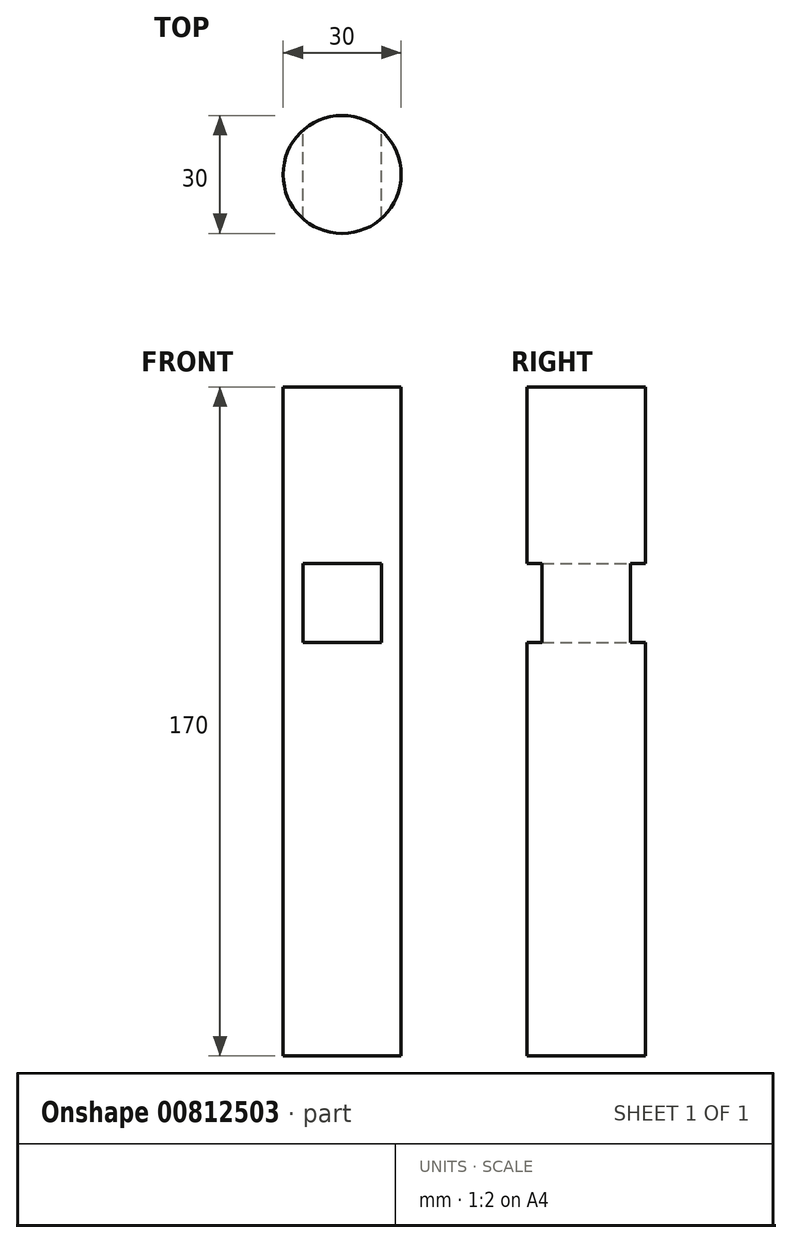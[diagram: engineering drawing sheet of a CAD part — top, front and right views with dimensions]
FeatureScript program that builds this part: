
annotation { "Feature Type Name" : "Feature", "Feature Type Description" : "" }
export const myFeature = defineFeature(function(context is Context, id is Id, definition is map)
    precondition{}
    {
        {
            var Q0;
            Q0=qCreatedBy(makeId("Top.planeOp"),FACE);
            var sketch = newSketch(context, id + "F0", { "sketchPlane" : qUnion([Q0])});
            skCircle(sketch, "E0", {"center": v(0, 0) * mm, "radius": 15 * mm});
            skSolve(sketch);
        }
        {
            var Q0;
            Q0 = qSketchRegion(id + "F0", true);
            extrude(context, id + "F1", {"entities" : qUnion([Q0]), "depth" : 120 * mm, "offsetDistance" : 25 * mm, "hasSecondDirection" : true, "secondDirectionOppositeDirection" : true, "secondDirectionDepth" : 50 * mm});
        }
        {
            var Q0;
            Q0=qCreatedBy(makeId("Front.planeOp"),FACE);
            var sketch = newSketch(context, id + "F2", { "sketchPlane" : qUnion([Q0])});
            skLineSegment(sketch, "E1.bottom", {"start": v(-10, 75.11) * mm, "end": v(10, 75.11) * mm});
            skLineSegment(sketch, "E1.top", {"start": v(-10, 55.11) * mm, "end": v(10, 55.11) * mm});
            skLineSegment(sketch, "E1.left", {"start": v(-10, 75.11) * mm, "end": v(-10, 55.11) * mm});
            skLineSegment(sketch, "E1.right", {"start": v(10, 75.11) * mm, "end": v(10, 55.11) * mm});
            skSolve(sketch);
        }
        {
            var Q0;
            Q0 = qSketchRegion(id + "F2", true);
            extrude(context, id + "F3", {"entities" : qUnion([Q0]), "operationType" : NewBodyOperationType.REMOVE, "endBound" : BoundingType.SYMMETRIC, "depth" : 100 * mm, "offsetDistance" : 25 * mm});
        }
    });
